# Revit family: Double Wave 800 Deep Add-on Unit
name_source: partatom
category: Furniture
revit_build: Autodesk Revit 2016 (Build: 20160525_1230(x64)
units: mm (PartAtom-declared; Revit-internal decimal feet)

## family parameters
Always vertical = Yes
Cut with Voids When Loaded = No
OmniClass Number = 23.40.20.00
OmniClass Title = General Furniture and Specialties
Room Calculation Point = No
Shared = No
Work Plane-Based = No

## types (3) — shared parameters
Assembly Code = E2020200
Desktop = Gresham - Nordic Ash
Foot = Gresham - Black Plastic
Frame = Gresham - Black Metal
Manufacturer = Gresham Office Furniture
Range = MESA
URL = www.gof.co.uk

## per-type parameters (varying)
| type | Product Code | Width |
| 1600 x 800 | MEFDW1608A | 1600 mm  [stored 5.24934 ft] |
| 1800 x 800 | MEFDW1808A | 1800 mm  [stored 5.90551 ft] |
| 2000 x 800 | MEFDW2008A | 2000 mm  [stored 6.56168 ft] |

note: [stored X ft] marks values corroborated as IEEE doubles in the binary element streams (Revit-internal decimal feet)

## geometry (parser evidence)
native form markers: Sweep x5
no freeform markers — native parametric forms only
